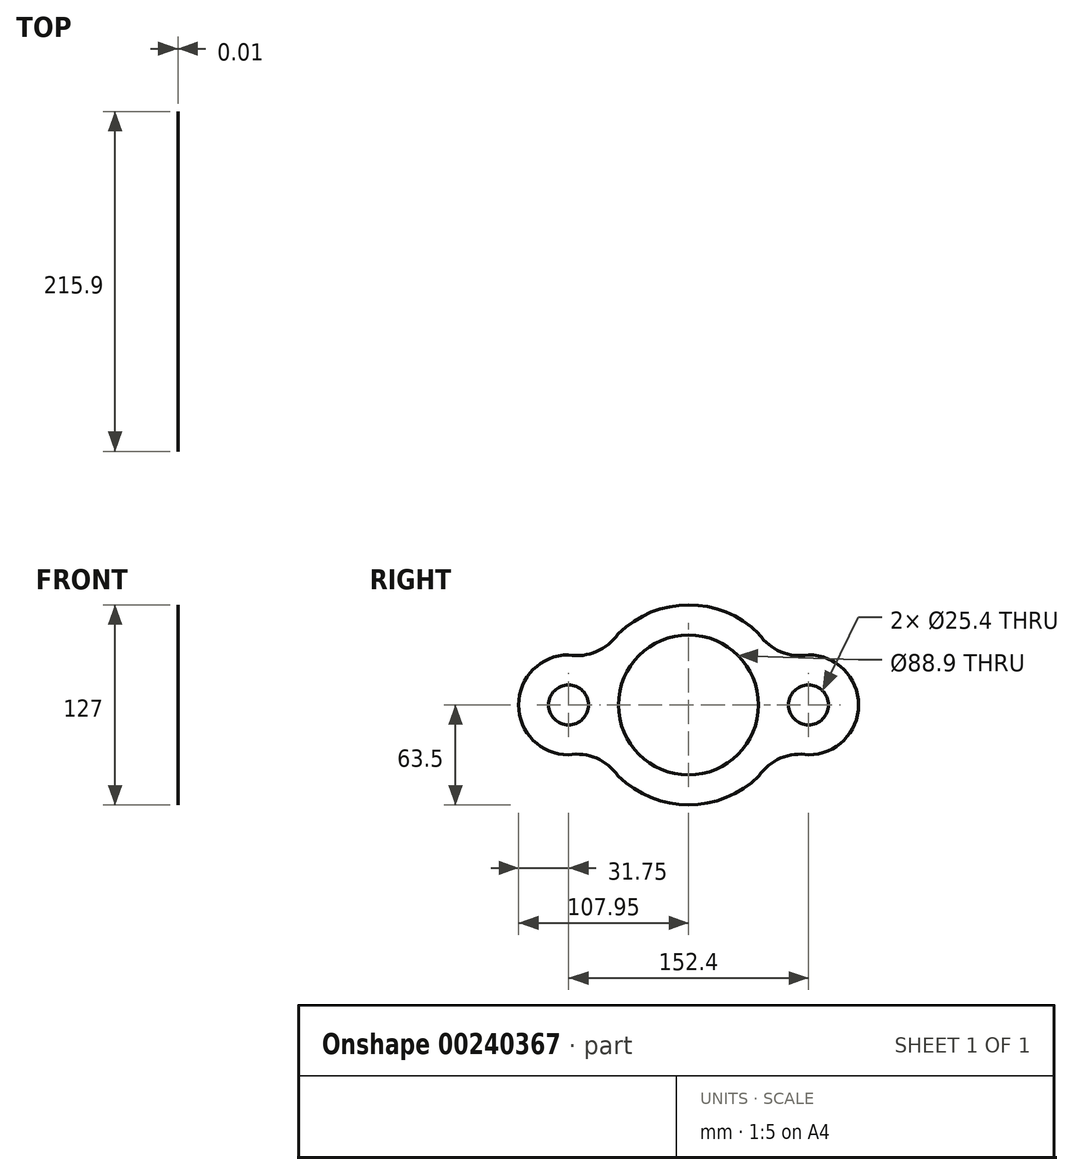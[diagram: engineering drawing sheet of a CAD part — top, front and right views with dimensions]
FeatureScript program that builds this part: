
annotation { "Feature Type Name" : "Feature", "Feature Type Description" : "" }
export const myFeature = defineFeature(function(context is Context, id is Id, definition is map)
    precondition{}
    {
        {
            var Q0;
            Q0=qCreatedBy(makeId("Right.planeOp"),FACE);
            var sketch = newSketch(context, id + "F0", { "sketchPlane" : qUnion([Q0])});
            skPoint(sketch, "E0.center.orphan", {"position": v(0, 31.48) * mm});
            skCircle(sketch, "E1", {"center": v(0, 0) * mm, "radius": 44.45 * mm});
            skCircle(sketch, "E2", {"center": v(-76.2, 0) * mm, "radius": 12.7 * mm});
            skCircle(sketch, "E3", {"center": v(76.2, 0) * mm, "radius": 12.7 * mm});
            skArc(sketch, "E4", {"start": v(44.7, 45.11) * mm, "mid": v(0, 63.5) * mm, "end": v(-44.7, 45.11) * mm});
            skLineSegment(sketch, "E5", {"start": v(44.64, 45.17) * mm, "end": v(45.2, 44.42) * mm});
            skArc(sketch, "E6", {"start": v(76.2, -31.75) * mm, "mid": v(107.95, 0) * mm, "end": v(76.2, 31.75) * mm});
            skLineSegment(sketch, "E7", {"start": v(-44.45, 0) * mm, "end": v(-44.45, 0) * mm});
            skArc(sketch, "E8.MirrorC", {"start": v(-76.2, -31.75) * mm, "mid": v(-107.95, 0) * mm, "end": v(-76.2, 31.75) * mm});
            skArc(sketch, "E9.MirrorC", {"start": v(-44.7, 45.11) * mm, "mid": v(0, 63.5) * mm, "end": v(44.7, 45.11) * mm});
            skLineSegment(sketch, "E10.trimOffspring", {"start": v(-57.94, 25.98) * mm, "end": v(-57.94, 25.98) * mm});
            skLineSegment(sketch, "E11.trimOffspring", {"start": v(-57.94, -25.98) * mm, "end": v(-57.94, -25.98) * mm});
            skArc(sketch, "E12.trimOffspring", {"start": v(44.7, -45.11) * mm, "mid": v(0, -63.5) * mm, "end": v(-44.7, -45.11) * mm});
            skArc(sketch, "E13.trimOffspring", {"start": v(-44.7, -45.11) * mm, "mid": v(0, -63.5) * mm, "end": v(44.7, -45.11) * mm});
            skArc(sketch, "E14.trimOffspring", {"start": v(-76.2, 31.75) * mm, "mid": v(-107.95, 0) * mm, "end": v(-76.2, -31.75) * mm});
            skArc(sketch, "E15", {"start": v(-76.2, 31.75) * mm, "mid": v(-58.5, 33.82) * mm, "end": v(-44.7, 45.11) * mm});
            skArc(sketch, "E16.MirrorCS", {"start": v(76.2, 31.75) * mm, "mid": v(58.5, 33.82) * mm, "end": v(44.7, 45.11) * mm});
            skArc(sketch, "E17.MirrorCS", {"start": v(-76.2, -31.75) * mm, "mid": v(-58.5, -33.82) * mm, "end": v(-44.7, -45.11) * mm});
            skArc(sketch, "E18.MirrorCS", {"start": v(76.2, -31.75) * mm, "mid": v(58.5, -33.82) * mm, "end": v(44.7, -45.11) * mm});
            skSolve(sketch);
        }
        {
            var Q0;
            Q0=makeQuery(id+"F0.imprint","IMPRINT",FACE,{"disambiguationData":[TD([[makeQuery(id+"F0.imprint","IMPRINT",EDGE,{"derivedFrom":sQuery(id+"F0.wireOp",EDGE,"E2")}),-1.0]])]});
            extrude(context, id + "F1", {"entities" : qUnion([Q0]), "depth" : 1 / 101.6 * mm});
        }
    });
